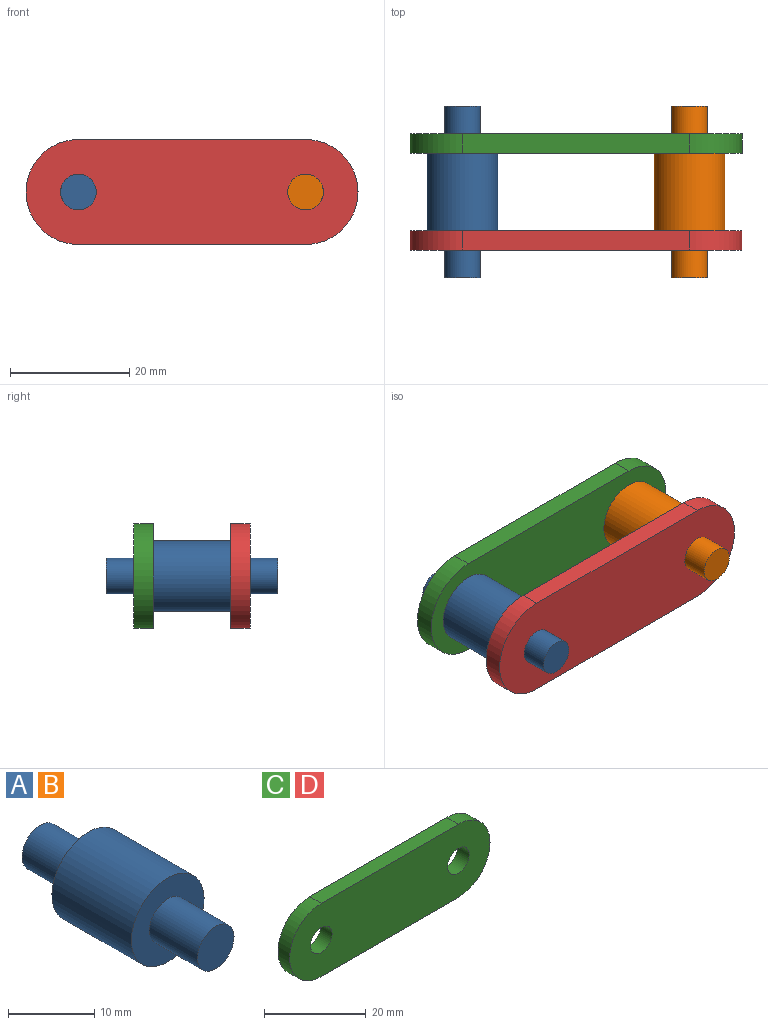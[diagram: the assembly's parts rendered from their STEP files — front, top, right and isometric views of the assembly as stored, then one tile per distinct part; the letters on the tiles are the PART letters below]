
ASSEMBLY  parts=4 mates=3
PART A: 7 faces, bbox 11.9x28.7x11.9 mm
  f0: cylinder r=5.95mm len=13mm, axis (0,-1,0), area 486mm2, adj f2,f5
  f1: cylinder r=3mm len=7.85mm, axis (0,-1,0), area 148mm2, adj f2,f3
  f2: plane 11.9x11.9mm, normal (0,-1,0), area 82.9mm2, adj f0,f1
  f3: plane 6x6mm, normal (0,-1,0), area 28.3mm2, adj f1
  f4: cylinder r=3mm len=7.85mm, axis (0,1,0), area 148mm2, adj f5,f6
  f5: plane 11.9x11.9mm, normal (0,1,0), area 82.9mm2, adj f0,f4
  f6: plane 6x6mm, normal (0,1,0), area 28.3mm2, adj f4
PART B: same geometry as A
PART C: 8 faces, bbox 55.7x3.3x17.6 mm
  f0: plane 38.1x3.25mm, normal (0,0,1), area 123.8mm2, adj f1,f4,f6,f7
  f1: cylinder r=8.8mm len=17.6mm, axis (0,1,0), area 89.8mm2, adj f0,f2,f6,f7
  f2: plane 38.1x3.25mm, normal (0,0,-1), area 123.8mm2, adj f1,f4,f6,f7
  f3: cylinder r=3mm len=6mm, axis (0,1,0), area 61.3mm2, adj f6,f7
  f4: cylinder r=8.8mm len=17.6mm, axis (0,1,0), area 89.8mm2, adj f0,f2,f6,f7
  f5: cylinder r=3mm len=6mm, axis (0,1,0), area 61.3mm2, adj f6,f7
  f6: plane 55.7x17.6mm, normal (0,-1,0), area 857.3mm2, adj f0,f1,f2,f3,f4,f5
  f7: plane 55.7x17.6mm, normal (0,1,0), area 857.3mm2, adj f0,f1,f2,f3,f4,f5
PART D: same geometry as C
PLACE A t=(-38.1,-6.5,0)mm fixed
PLACE B t=(0,-6.5,0)mm
PLACE C rot(axis=(1,0,0),180deg) t=(0,6.5,0)mm
PLACE D rot(axis=(1,0,0),180deg) t=(0,-9.75,0)mm
MATE fastened B.f1 <-> D.f3  axis (0,-1,0) through (38.1,-6.5,0)mm
MATE fastened C.f3 <-> B.f1  axis (0,-1,0) through (38.1,6.5,0)mm
MATE fastened D.f1 <-> A.f1  axis (0,-1,0) through (0,-6.5,0)mm
